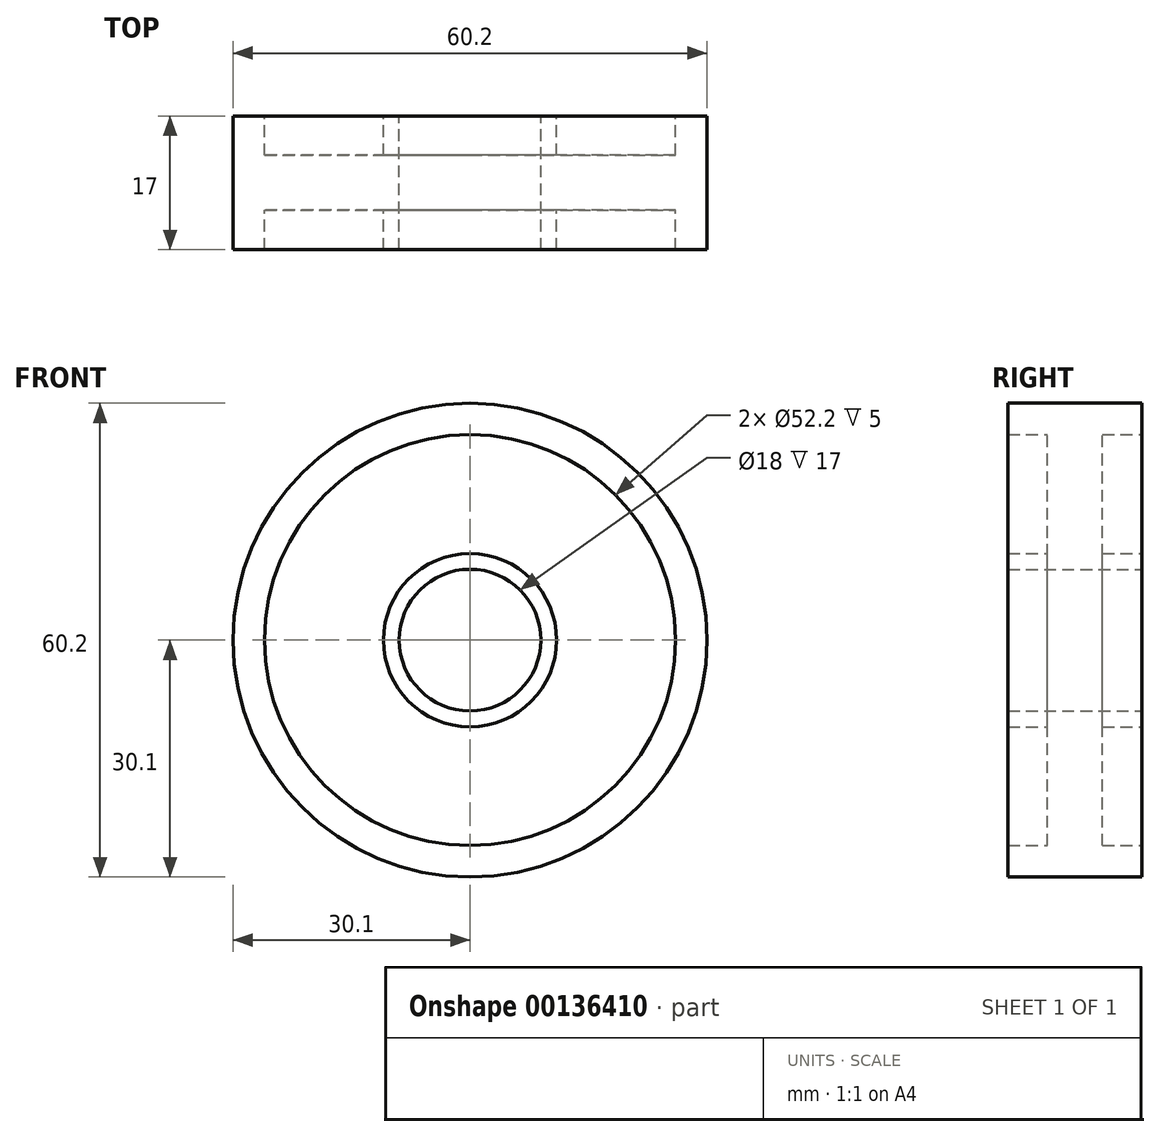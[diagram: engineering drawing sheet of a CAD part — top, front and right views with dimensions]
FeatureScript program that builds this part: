
annotation { "Feature Type Name" : "Feature", "Feature Type Description" : "" }
export const myFeature = defineFeature(function(context is Context, id is Id, definition is map)
    precondition{}
    {
        {
            var Q0;
            Q0=qCreatedBy(makeId("Front.planeOp"),FACE);
            var sketch = newSketch(context, id + "F0", { "sketchPlane" : qUnion([Q0])});
            skCircle(sketch, "E0", {"center": v(0, 0) * mm, "radius": 26.1 * mm});
            skCircle(sketch, "E1", {"center": v(0, 0) * mm, "radius": 30.1 * mm});
            skCircle(sketch, "E2", {"center": v(0, 0) * mm, "radius": 11 * mm});
            skCircle(sketch, "E3", {"center": v(0, 0) * mm, "radius": 9 * mm});
            skSolve(sketch);
        }
        {
            var Q0;
            Q0=makeQuery(id+"F0.imprint","IMPRINT",FACE,{"disambiguationData":[TD([[makeQuery(id+"F0.imprint","IMPRINT",EDGE,{"derivedFrom":sQuery(id+"F0.wireOp",EDGE,"E2")}),1.0]])]});
            extrude(context, id + "F1", {"entities" : qUnion([Q0]), "endBound" : BoundingType.SYMMETRIC, "depth" : 17 * mm});
        }
        {
            var Q0;
            Q0=makeQuery(id+"F0.imprint","IMPRINT",FACE,{"disambiguationData":[TD([[makeQuery(id+"F0.imprint","IMPRINT",EDGE,{"derivedFrom":sQuery(id+"F0.wireOp",EDGE,"E0")}),1.0]])]});
            extrude(context, id + "F2", {"entities" : qUnion([Q0]), "operationType" : NewBodyOperationType.ADD, "endBound" : BoundingType.SYMMETRIC, "depth" : 7 * mm});
        }
        {
            var Q0;
            Q0=makeQuery(id+"F0.imprint","IMPRINT",FACE,{"disambiguationData":[TD([[makeQuery(id+"F0.imprint","IMPRINT",EDGE,{"derivedFrom":sQuery(id+"F0.wireOp",EDGE,"E0")}),-1.0]])]});
            extrude(context, id + "F3", {"entities" : qUnion([Q0]), "operationType" : NewBodyOperationType.ADD, "endBound" : BoundingType.SYMMETRIC, "depth" : 17 * mm});
        }
    });
